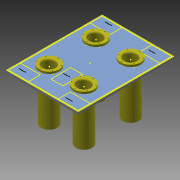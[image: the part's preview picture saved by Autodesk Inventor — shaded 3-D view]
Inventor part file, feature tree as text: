
AUTODESK INVENTOR PART (.ipt)
format: ipt  version: 2015 (Build 190159000, 159)  size: 416,768 bytes
history: native  units: in
note: dims shown in document units (in); Inventor stores cm internally (conversion verified against a paired STEP export)
features: thread x25, other x10, sketch x6, plane x3, extrude x3, mirror x3, hole x2, pattern_circular x1, fillet x1, projected_geometry x1
ambient origin geometry x8: Origin, YZ Plane, XZ Plane, XY Plane, X Axis, Y Axis, Z Axis, Center Point
bodies: Solid3 (feature_tree), Solid4 (feature_tree), Solid5 (feature_tree)
feature tree (55):
  other  "board_with_hole_pipes.ipt"
  other  "Layout with const "
  plane  "Work Plane1"
  extrude  "Extrusion1"  Depth=18.0in
  extrude  "Extrusion2"  Depth=24.0in
  hole  "Hole1"  [1 undecoded]
  thread  "Thread1"  [1 undecoded]
  pattern_circular  "Circular Pattern1"  [2 undecoded]
  fillet  "Fillet1"  Radius=4.0in
  plane  "Work Plane3"
  hole  "Hole2"  [1 undecoded]
  thread  "Thread2"  [1 undecoded]
  thread  "Thread3"  [1 undecoded]
  thread  "Thread4"  [1 undecoded]
  thread  "Thread5"  [1 undecoded]
  thread  "Thread6"  [1 undecoded]
  thread  "Thread7"  [1 undecoded]
  mirror  "Mirror1"
  mirror  "Mirror2"
  mirror  "Mirror3"
  plane  "Work Plane4"
  extrude  "Extrusion3"  Depth=0.4375in
  other  "simple layout"
  thread  "Thread8"  [1 undecoded]
  thread  "Thread9"  [1 undecoded]
  thread  "Thread10"  [1 undecoded]
  thread  "Thread11"  [1 undecoded]
  thread  "Thread12"  [1 undecoded]
  thread  "Thread13"  [1 undecoded]
  thread  "Thread14"  [1 undecoded]
  thread  "Thread15"  [1 undecoded]
  thread  "Thread16"  [1 undecoded]
  thread  "Thread17"  [1 undecoded]
  thread  "Thread18"  [1 undecoded]
  thread  "Thread19"  [1 undecoded]
  thread  "Thread20"  [1 undecoded]
  thread  "Thread21"  [1 undecoded]
  thread  "Thread22"  [1 undecoded]
  thread  "Thread23"  [1 undecoded]
  thread  "Thread24"  [1 undecoded]
  thread  "Thread25"  [1 undecoded]
  other  "Solid1::board_with_hole_pipes.ipt"
  other  "TaggingFeature1"
  sketch  "Sketch3"  dims[d0=0.1969in d1=18.0in]
  sketch  "Sketch4"  dims[d2=24.0in d3=23.5in]
  other  "leg"
  sketch  "Sketch5"  dims[d4=17.5in d5=5.5in d6=1.5in]
  sketch  "Sketch6"  dims[d9=5.5in]
  sketch  "Sketch7"  dims[d10=1.5in]
  other  "Pattern of leg:1"
  other  "Pattern of leg:2"
  other  "Pattern of Solid3:3"
  sketch  "Sketch8"  dims[d11=5.5in d12=1.5in d15=4.0in d18=5.5in d19=1.5in d22=5.0in d23=3.0in d24=5.0in d25=3.0in d26=3.0in d27=3.0in d28=3.0in d29=5.0in d30=4.0in d31=3.0in d32=0.5in d33=12.0in d34=0.0in d35=0.0in d36=5.0in d37=0.5in d38=0.0in d39=0.25in d40=0.75in d41=0.375in d42=0.25in d43=0.5635in d44=1.8125in d45=0.8108in d46=1.0in d47=0.0in d48=2.3622in d49=360.0deg d51=0.4375in d52=0.25in d53=0.75in d54=0.375in d55=0.25in d56=0.5635in d57=1.8125in d58=0.8108in d59=1.0in d60=0.0in d61=1.0in d62=0.0in d63=1.0in d64=0.0in d65=1.0in d66=0.0in d67=1.0in d68=0.0in d69=1.0in d70=0.0in d71=3.475in d72=0.0in d73=1.0in d74=0.0in d75=1.0in d76=0.0in d77=1.0in d78=0.0in d79=1.0in d80=0.0in d81=1.0in d82=0.0in d83=1.0in d84=0.0in d85=1.0in d86=0.0in d87=1.0in d88=0.0in d89=1.0in d90=0.0in d91=1.0in d92=0.0in d93=1.0in d94=0.0in d95=1.0in d96=0.0in d97=1.0in d98=0.0in d99=1.0in d100=0.0in d101=1.0in d102=0.0in d103=1.0in d104=0.0in d105=1.0in d106=0.0in d107=1.0in d108=0.0in]
  projected_geometry  "Projected Loop2"
  other  "platform"
note: 29 required parameter values undecoded (feature->parameter linkage not recoverable at this tier; creation-order binding heuristic only, values carry confidence <= 0.55)
